# Revit family: 305_77c2d52564984d969c66b6215357ec
name_source: partatom
category: Pipe Accessories
revit_build: Autodesk Revit 2018 (Build: 20170223_1515(x64)
units: mm (PartAtom-declared; Revit-internal decimal feet)

## family parameters
Always vertical = Yes
Cut with Voids When Loaded = No
Part Type = Valve - Breaks Into
Round Connector Dimension = Use Diameter
Shared = No
Work Plane-Based = No

## types (6) — shared parameters
CAT0 = Yes
Description = Bronze full port gate valve PN16
L2D = 49 mm
L2D_Min = 3048 mm
Manufacturer = VIR
QmdConnectorList = 301;D;302;D
URL = http://www.vironline.com
W2D = 15 mm  [stored 0.0492126 ft]
magiPartTypeId = 305
magiProductFamilyId = 77c2d52564984d969c66b6215357ec

## per-type parameters (varying)
| type | CenSd_R3_6 | D | H | H1 | H1__ve | H2 | H5 | H6 | H6__ve | L1 | L2 | L2__ve | L3 | L3__ve | L_2 | R1 | R2 | R3 | R4 | R5 | R6 | W_2 | magiProductId |
| 90 DN15 | 13 mm  [stored 0.0426509 ft] | 15 mm | 66 mm | 18 mm  [stored 0.0590551 ft] | -18 mm | 10 mm  [stored 0.0328084 ft] | 35 mm | 13 mm  [stored 0.0426509 ft] | -13 mm | 7 mm  [stored 0.0229659 ft] | 8 mm  [stored 0.0262467 ft] | -8 mm | 10 mm  [stored 0.0328084 ft] | -10 mm  [stored -0.0328084 ft] | 25 mm  [stored 0.082021 ft] | 13 mm  [stored 0.0426509 ft] | 12 mm  [stored 0.0393701 ft] | 15 mm  [stored 0.0492126 ft] | 30 mm  [stored 0.0984252 ft] | 6 mm  [stored 0.019685 ft] | 16 mm  [stored 0.0524934 ft] | 13 mm  [stored 0.0426509 ft] | b929f3006f964561a71ab34b04ff15 |
| 90 DN20 | 15 mm  [stored 0.0492126 ft] | 20 mm | 77 mm | 22 mm | -22 mm  [stored -0.0721785 ft] | 11 mm | 40 mm | 15 mm  [stored 0.0492126 ft] | -15 mm | 7 mm  [stored 0.0229659 ft] | 8 mm  [stored 0.0262467 ft] | -8 mm | 11 mm | -11 mm | 26 mm  [stored 0.0853018 ft] | 16 mm  [stored 0.0524934 ft] | 15 mm  [stored 0.0492126 ft] | 18 mm  [stored 0.0590551 ft] | 30 mm  [stored 0.0984252 ft] | 6 mm  [stored 0.019685 ft] | 18 mm  [stored 0.0590551 ft] | 16 mm  [stored 0.0524934 ft] | 33303340ac1f4837b6928fe12a754d |
| 90 DN25 | 19 mm  [stored 0.062336 ft] | 25 mm | 89 mm | 27 mm  [stored 0.0885827 ft] | -27 mm  [stored -0.0885827 ft] | 12 mm  [stored 0.0393701 ft] | 46 mm | 17 mm | -17 mm  [stored -0.0557743 ft] | 9 mm  [stored 0.0295276 ft] | 10 mm  [stored 0.0328084 ft] | -10 mm  [stored -0.0328084 ft] | 13 mm  [stored 0.0426509 ft] | -13 mm | 31 mm | 19 mm  [stored 0.062336 ft] | 18 mm  [stored 0.0590551 ft] | 22 mm | 35 mm | 7 mm  [stored 0.0229659 ft] | 22 mm | 19 mm  [stored 0.062336 ft] | 4f1ae8f74cda4892811519e19d9701 |
| 90 DN32 | 24 mm  [stored 0.0787402 ft] | 32 mm | 111 mm | 34 mm | -34 mm | 15 mm  [stored 0.0492126 ft] | 57 mm | 21 mm  [stored 0.0688976 ft] | -21 mm | 10 mm  [stored 0.0328084 ft] | 12 mm  [stored 0.0393701 ft] | -12 mm  [stored -0.0393701 ft] | 14 mm  [stored 0.0459318 ft] | -14 mm | 35 mm | 24 mm  [stored 0.0787402 ft] | 23 mm | 28 mm | 43 mm | 7 mm  [stored 0.0229659 ft] | 27 mm  [stored 0.0885827 ft] | 24 mm  [stored 0.0787402 ft] | eb9e9e34930745828d03561bba8367 |
| 90 DN40 | 27 mm  [stored 0.0885827 ft] | 40 mm | 124 mm | 38 mm | -38 mm | 17 mm | 63 mm | 23 mm | -23 mm | 10 mm  [stored 0.0328084 ft] | 13 mm  [stored 0.0426509 ft] | -13 mm | 14 mm  [stored 0.0459318 ft] | -14 mm | 36 mm | 27 mm  [stored 0.0885827 ft] | 26 mm  [stored 0.0853018 ft] | 31 mm | 43 mm | 8 mm  [stored 0.0262467 ft] | 30 mm  [stored 0.0984252 ft] | 27 mm  [stored 0.0885827 ft] | d9dc5ec4ca574d79b1117fc2986330 |
| 90 DN50 | 33 mm | 50 mm | 143 mm | 47 mm | -47 mm | 19 mm  [stored 0.062336 ft] | 70 mm | 26 mm  [stored 0.0853018 ft] | -26 mm | 12 mm  [stored 0.0393701 ft] | 14 mm  [stored 0.0459318 ft] | -14 mm | 17 mm | -17 mm  [stored -0.0557743 ft] | 42 mm | 34 mm | 32 mm | 39 mm | 50 mm | 9 mm  [stored 0.0295276 ft] | 37 mm | 34 mm | 4a2fe0a3a93844cf9650f174275ae4 |

note: column(s) folded — value = type name in every type: MC Product Code

note: [stored X ft] marks values corroborated as IEEE doubles in the binary element streams (Revit-internal decimal feet)
